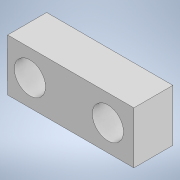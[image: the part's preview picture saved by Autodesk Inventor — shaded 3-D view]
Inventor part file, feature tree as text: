
AUTODESK INVENTOR PART (.ipt)
format: ipt  version: 2020 (Build 240168000, 168)  size: 113,152 bytes
history: native  units: in
note: dims shown in document units (in); Inventor stores cm internally (conversion verified against a paired STEP export)
features: sketch x2, extrude x1, hole x1
ambient origin geometry x8: Origin, YZ Plane, XZ Plane, XY Plane, X Axis, Y Axis, Z Axis, Center Point
bodies: Solid1 (feature_tree)
feature tree (4):
  extrude  "Extrusion1"  Depth=0.5906in
  hole  "Hole1"  [1 undecoded]
  sketch  "Sketch1"  dims[d4=0.5906in d5=0.0in d6=0.2047in]
  sketch  "Sketch2"  dims[d7=0.3937in d8=0.3937in d9=0.2047in d10=0.3937in d11=1.1811in d12=0.2047in d13=0.2362in d14=0.4724in d15=0.4724in d16=90.0deg d17=0.315in d18=0.8108in d19=0.3937in d20=0.3937in d21=0.0in]
note: 1 required parameter value undecoded (feature->parameter linkage not recoverable at this tier; creation-order binding heuristic only, values carry confidence <= 0.55)
